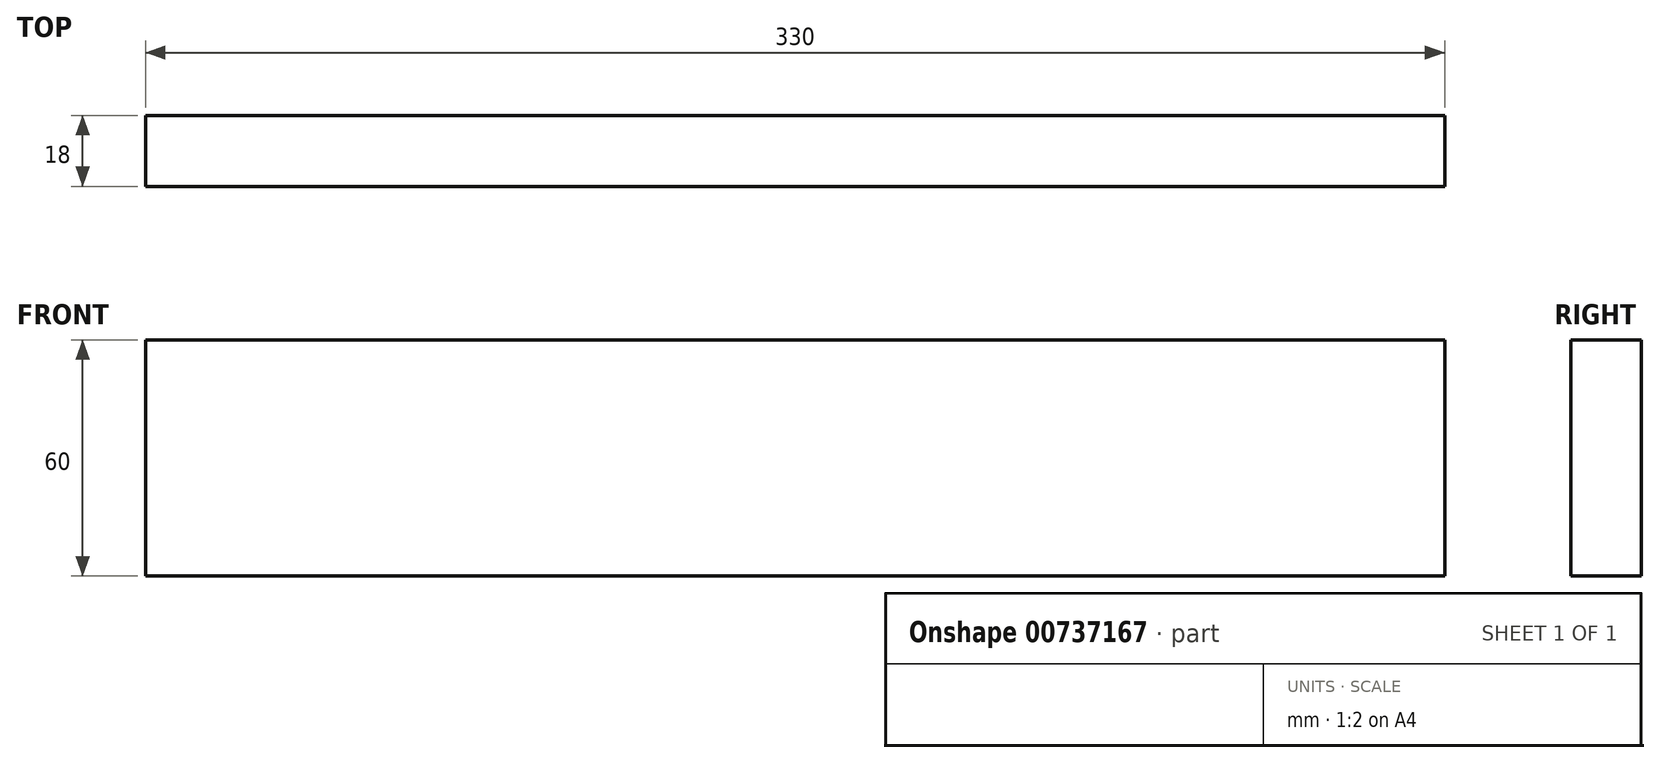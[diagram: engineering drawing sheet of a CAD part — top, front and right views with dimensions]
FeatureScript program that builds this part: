
annotation { "Feature Type Name" : "Feature", "Feature Type Description" : "" }
export const myFeature = defineFeature(function(context is Context, id is Id, definition is map)
    precondition{}
    {
        {
            var Q0;
            Q0=qCreatedBy(makeId("Front.planeOp"),FACE);
            var sketch = newSketch(context, id + "F0", { "sketchPlane" : qUnion([Q0])});
            skLineSegment(sketch, "E0.bottom", {"start": v(165, 30) * mm, "end": v(-165, 30) * mm});
            skLineSegment(sketch, "E0.top", {"start": v(165, -30) * mm, "end": v(-165, -30) * mm});
            skLineSegment(sketch, "E0.left", {"start": v(165, 30) * mm, "end": v(165, -30) * mm});
            skLineSegment(sketch, "E0.right", {"start": v(-165, 30) * mm, "end": v(-165, -30) * mm});
            skPoint(sketch, "E0.middle", {"position": v(0, 0) * mm});
            skSolve(sketch);
        }
        {
            var Q0;
            Q0 = qSketchRegion(id + "F0", true);
            extrude(context, id + "F1", {"entities" : qUnion([Q0]), "endBound" : BoundingType.SYMMETRIC, "depth" : 18 * mm, "offsetDistance" : 25 * mm});
        }
    });
